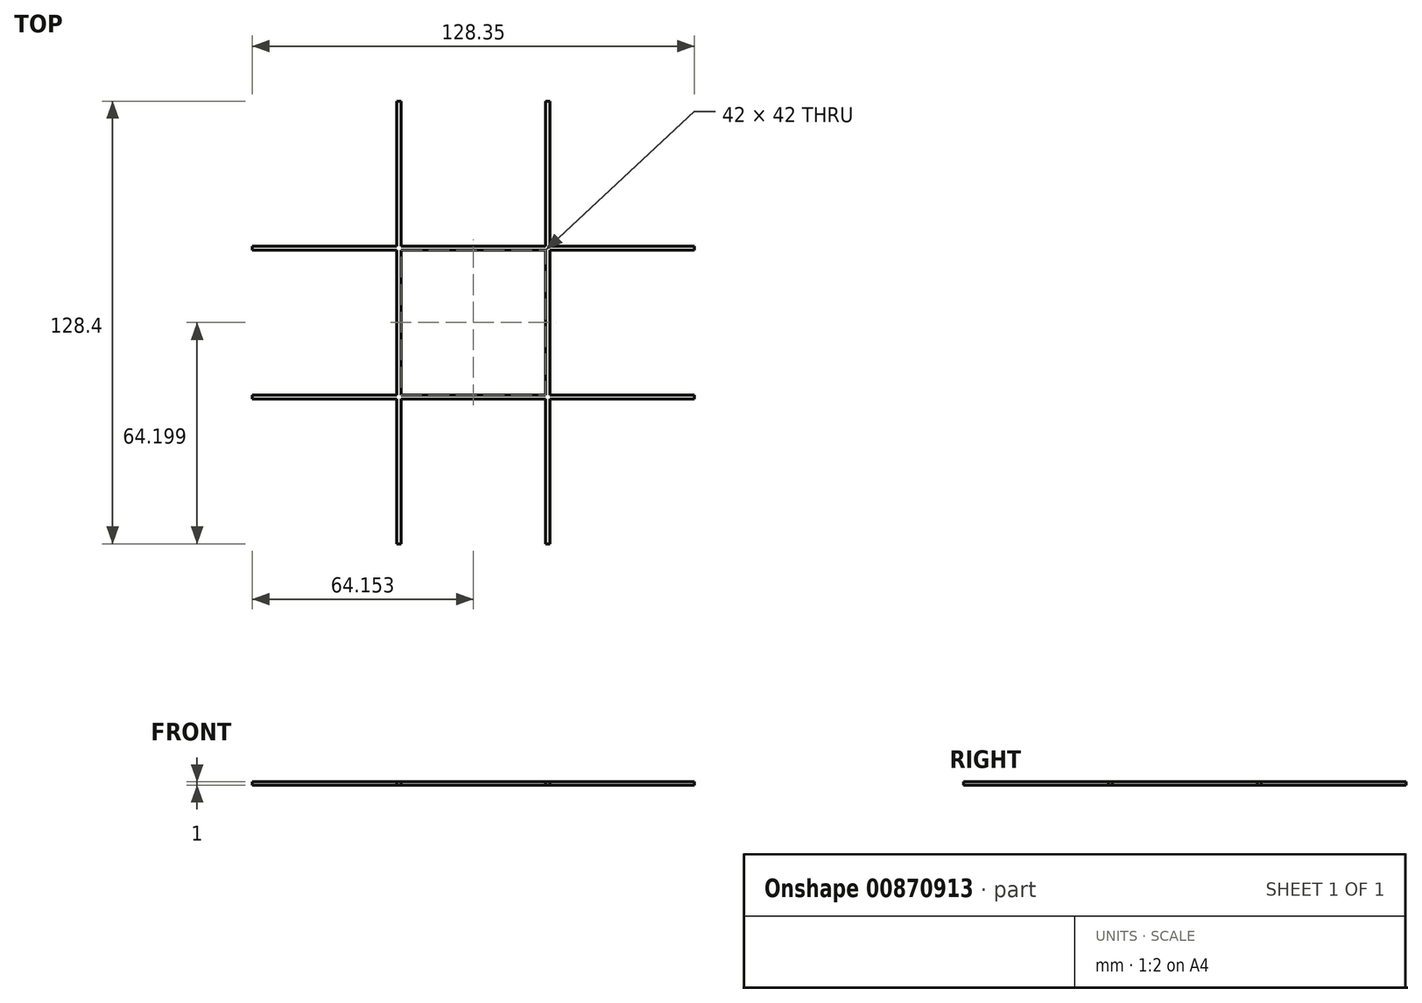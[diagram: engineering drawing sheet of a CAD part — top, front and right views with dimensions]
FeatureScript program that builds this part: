
annotation { "Feature Type Name" : "Feature", "Feature Type Description" : "" }
export const myFeature = defineFeature(function(context is Context, id is Id, definition is map)
    precondition{}
    {
        {
            var Q0;
            Q0=qCreatedBy(makeId("Top.planeOp"),FACE);
            var sketch = newSketch(context, id + "F0", { "sketchPlane" : qUnion([Q0])});
            skLineSegment(sketch, "E0.bottom", {"start": v(-34.17, 34.2) * mm, "end": v(7.83, 34.2) * mm});
            skLineSegment(sketch, "E0.top", {"start": v(-34.17, -7.8) * mm, "end": v(7.83, -7.8) * mm});
            skLineSegment(sketch, "E0.left", {"start": v(-34.17, 34.2) * mm, "end": v(-34.17, -7.8) * mm});
            skLineSegment(sketch, "E0.right", {"start": v(7.83, 34.2) * mm, "end": v(7.83, -7.8) * mm});
            skLineSegment(sketch, "E1.bottom", {"start": v(-35.37, 35.4) * mm, "end": v(9.03, 35.4) * mm});
            skLineSegment(sketch, "E1.top", {"start": v(-35.37, -9) * mm, "end": v(9.03, -9) * mm});
            skLineSegment(sketch, "E1.left", {"start": v(-35.37, 35.4) * mm, "end": v(-35.37, -9) * mm});
            skLineSegment(sketch, "E1.right", {"start": v(9.03, 35.4) * mm, "end": v(9.03, -9) * mm});
            skSolve(sketch);
        }
        {
            var Q0;
            Q0=makeQuery(id+"F0.imprint","IMPRINT",FACE,{"disambiguationData":[TD([[makeQuery(id+"F0.imprint","IMPRINT",EDGE,{"derivedFrom":sQuery(id+"F0.wireOp",EDGE,"E0.bottom")}),1.0]])]});
            extrude(context, id + "F1", {"entities" : qUnion([Q0]), "depth" : 1 * mm, "offsetDistance" : 25.4 * mm});
        }
        {
            var Q0;
            Q0=makeQuery(id+"F1.opExtrude","SWEPT_BODY",BODY,{"disambiguationData":[OSD([sQuery(id+"F0.wireOp",EDGE,"E0.bottom"),sQuery(id+"F0.wireOp",EDGE,"E0.top"),sQuery(id+"F0.wireOp",EDGE,"E0.left"),sQuery(id+"F0.wireOp",EDGE,"E0.right"),sQuery(id+"F0.wireOp",EDGE,"E1.bottom"),sQuery(id+"F0.wireOp",EDGE,"E1.top"),sQuery(id+"F0.wireOp",EDGE,"E1.left"),sQuery(id+"F0.wireOp",EDGE,"E1.right")])]});
            transform(context, id + "F2", {"entities" : qUnion([Q0]), "transformType" : TransformType.TRANSLATION_3D, "dx" : 43.2 * mm, "dy" : 0 * mm, "dz" : 0 * mm, "makeCopy" : true});
        }
        {
            var Q0;
            Q0=makeQuery(id+"F2.opPattern","COPY",BODY,{"derivedFrom":makeQuery(id+"Fn17MzBWq50HigD_0.opExtrude","SWEPT_BODY",BODY,{"disambiguationData":[OSD([sQuery(id+"F0.wireOp",EDGE,"E0.bottom"),sQuery(id+"F0.wireOp",EDGE,"E0.top"),sQuery(id+"F0.wireOp",EDGE,"E0.left"),sQuery(id+"F0.wireOp",EDGE,"E0.right"),sQuery(id+"F0.wireOp",EDGE,"E1.bottom"),sQuery(id+"F0.wireOp",EDGE,"E1.top"),sQuery(id+"F0.wireOp",EDGE,"E1.left"),sQuery(id+"F0.wireOp",EDGE,"E1.right")])]}),"instanceName":"1"});
            var Q1;
            Q1=makeQuery(id+"F2.opPattern","COPY",BODY,{"derivedFrom":makeQuery(id+"F1.opExtrude","SWEPT_BODY",BODY,{"disambiguationData":[OSD([sQuery(id+"F0.wireOp",EDGE,"E0.bottom"),sQuery(id+"F0.wireOp",EDGE,"E0.top"),sQuery(id+"F0.wireOp",EDGE,"E0.left"),sQuery(id+"F0.wireOp",EDGE,"E0.right"),sQuery(id+"F0.wireOp",EDGE,"E1.bottom"),sQuery(id+"F0.wireOp",EDGE,"E1.top"),sQuery(id+"F0.wireOp",EDGE,"E1.left"),sQuery(id+"F0.wireOp",EDGE,"E1.right")])]}),"instanceName":"1"});
            transform(context, id + "F3", {"entities" : qUnion([Q0, Q1]), "transformType" : TransformType.TRANSLATION_3D, "dx" : 43.2 * mm, "dy" : 0 * mm, "dz" : 0 * mm, "makeCopy" : true});
        }
        {
            var Q0;
            Q0=makeQuery(id+"F1.opExtrude","SWEPT_BODY",BODY,{"disambiguationData":[OSD([sQuery(id+"F0.wireOp",EDGE,"E0.bottom"),sQuery(id+"F0.wireOp",EDGE,"E0.top"),sQuery(id+"F0.wireOp",EDGE,"E0.left"),sQuery(id+"F0.wireOp",EDGE,"E0.right"),sQuery(id+"F0.wireOp",EDGE,"E1.bottom"),sQuery(id+"F0.wireOp",EDGE,"E1.top"),sQuery(id+"F0.wireOp",EDGE,"E1.left"),sQuery(id+"F0.wireOp",EDGE,"E1.right")])]});
            var Q1;
            Q1=makeQuery(id+"F2.opPattern","COPY",BODY,{"derivedFrom":makeQuery(id+"F1.opExtrude","SWEPT_BODY",BODY,{"disambiguationData":[OSD([sQuery(id+"F0.wireOp",EDGE,"E0.bottom"),sQuery(id+"F0.wireOp",EDGE,"E0.top"),sQuery(id+"F0.wireOp",EDGE,"E0.left"),sQuery(id+"F0.wireOp",EDGE,"E0.right"),sQuery(id+"F0.wireOp",EDGE,"E1.bottom"),sQuery(id+"F0.wireOp",EDGE,"E1.top"),sQuery(id+"F0.wireOp",EDGE,"E1.left"),sQuery(id+"F0.wireOp",EDGE,"E1.right")])]}),"instanceName":"1"});
            var Q2;
            Q2=makeQuery(id+"F3.opPattern","COPY",BODY,{"derivedFrom":makeQuery(id+"F2.opPattern","COPY",BODY,{"derivedFrom":makeQuery(id+"F1.opExtrude","SWEPT_BODY",BODY,{"disambiguationData":[OSD([sQuery(id+"F0.wireOp",EDGE,"E0.bottom"),sQuery(id+"F0.wireOp",EDGE,"E0.top"),sQuery(id+"F0.wireOp",EDGE,"E0.left"),sQuery(id+"F0.wireOp",EDGE,"E0.right"),sQuery(id+"F0.wireOp",EDGE,"E1.bottom"),sQuery(id+"F0.wireOp",EDGE,"E1.top"),sQuery(id+"F0.wireOp",EDGE,"E1.left"),sQuery(id+"F0.wireOp",EDGE,"E1.right")])]}),"instanceName":"1"}),"instanceName":"1"});
            booleanBodies(context, id + "F4", {"operationType" : BooleanOperationType.UNION, "tools" : qUnion([Q0, Q1, Q2])});
        }
        {
            var Q0;
            Q0=makeQuery(id+"F1.opExtrude","SWEPT_BODY",BODY,{"disambiguationData":[OSD([sQuery(id+"F0.wireOp",EDGE,"E0.bottom"),sQuery(id+"F0.wireOp",EDGE,"E0.top"),sQuery(id+"F0.wireOp",EDGE,"E0.left"),sQuery(id+"F0.wireOp",EDGE,"E0.right"),sQuery(id+"F0.wireOp",EDGE,"E1.bottom"),sQuery(id+"F0.wireOp",EDGE,"E1.top"),sQuery(id+"F0.wireOp",EDGE,"E1.left"),sQuery(id+"F0.wireOp",EDGE,"E1.right")])]});
            transform(context, id + "F5", {"entities" : qUnion([Q0]), "transformType" : TransformType.TRANSLATION_3D, "dx" : 0 * mm, "dy" : 43.2 * mm, "dz" : 0 * mm, "makeCopy" : true});
        }
        {
            var Q0;
            Q0=makeQuery(id+"F5.opPattern","COPY",BODY,{"derivedFrom":makeQuery(id+"Fn17MzBWq50HigD_0.opExtrude","SWEPT_BODY",BODY,{"disambiguationData":[OSD([sQuery(id+"F0.wireOp",EDGE,"E0.bottom"),sQuery(id+"F0.wireOp",EDGE,"E0.top"),sQuery(id+"F0.wireOp",EDGE,"E0.left"),sQuery(id+"F0.wireOp",EDGE,"E0.right"),sQuery(id+"F0.wireOp",EDGE,"E1.bottom"),sQuery(id+"F0.wireOp",EDGE,"E1.top"),sQuery(id+"F0.wireOp",EDGE,"E1.left"),sQuery(id+"F0.wireOp",EDGE,"E1.right")])]}),"instanceName":"1"});
            var Q1;
            Q1=makeQuery(id+"F5.opPattern","COPY",BODY,{"derivedFrom":makeQuery(id+"F1.opExtrude","SWEPT_BODY",BODY,{"disambiguationData":[OSD([sQuery(id+"F0.wireOp",EDGE,"E0.bottom"),sQuery(id+"F0.wireOp",EDGE,"E0.top"),sQuery(id+"F0.wireOp",EDGE,"E0.left"),sQuery(id+"F0.wireOp",EDGE,"E0.right"),sQuery(id+"F0.wireOp",EDGE,"E1.bottom"),sQuery(id+"F0.wireOp",EDGE,"E1.top"),sQuery(id+"F0.wireOp",EDGE,"E1.left"),sQuery(id+"F0.wireOp",EDGE,"E1.right")])]}),"instanceName":"1"});
            transform(context, id + "F6", {"entities" : qUnion([Q0, Q1]), "transformType" : TransformType.TRANSLATION_3D, "dx" : 0 * mm, "dy" : 43.2 * mm, "dz" : 0 * mm, "makeCopy" : true});
        }
        {
            var Q0;
            Q0=makeQuery(id+"F1.opExtrude","SWEPT_BODY",BODY,{"disambiguationData":[OSD([sQuery(id+"F0.wireOp",EDGE,"E0.bottom"),sQuery(id+"F0.wireOp",EDGE,"E0.top"),sQuery(id+"F0.wireOp",EDGE,"E0.left"),sQuery(id+"F0.wireOp",EDGE,"E0.right"),sQuery(id+"F0.wireOp",EDGE,"E1.bottom"),sQuery(id+"F0.wireOp",EDGE,"E1.top"),sQuery(id+"F0.wireOp",EDGE,"E1.left"),sQuery(id+"F0.wireOp",EDGE,"E1.right")])]});
            var Q1;
            Q1=makeQuery(id+"F5.opPattern","COPY",BODY,{"derivedFrom":makeQuery(id+"F1.opExtrude","SWEPT_BODY",BODY,{"disambiguationData":[OSD([sQuery(id+"F0.wireOp",EDGE,"E0.bottom"),sQuery(id+"F0.wireOp",EDGE,"E0.top"),sQuery(id+"F0.wireOp",EDGE,"E0.left"),sQuery(id+"F0.wireOp",EDGE,"E0.right"),sQuery(id+"F0.wireOp",EDGE,"E1.bottom"),sQuery(id+"F0.wireOp",EDGE,"E1.top"),sQuery(id+"F0.wireOp",EDGE,"E1.left"),sQuery(id+"F0.wireOp",EDGE,"E1.right")])]}),"instanceName":"1"});
            var Q2;
            Q2=makeQuery(id+"F6.opPattern","COPY",BODY,{"derivedFrom":makeQuery(id+"F5.opPattern","COPY",BODY,{"derivedFrom":makeQuery(id+"F1.opExtrude","SWEPT_BODY",BODY,{"disambiguationData":[OSD([sQuery(id+"F0.wireOp",EDGE,"E0.bottom"),sQuery(id+"F0.wireOp",EDGE,"E0.top"),sQuery(id+"F0.wireOp",EDGE,"E0.left"),sQuery(id+"F0.wireOp",EDGE,"E0.right"),sQuery(id+"F0.wireOp",EDGE,"E1.bottom"),sQuery(id+"F0.wireOp",EDGE,"E1.top"),sQuery(id+"F0.wireOp",EDGE,"E1.left"),sQuery(id+"F0.wireOp",EDGE,"E1.right")])]}),"instanceName":"1"}),"instanceName":"1"});
            booleanBodies(context, id + "F7", {"operationType" : BooleanOperationType.UNION, "tools" : qUnion([Q0, Q1, Q2])});
        }
        {
            var Q0;
            {var subQ0=makeQuery(id+"F1.opExtrude","CAP_FACE",FACE,{"disambiguationData":[OSD([sQuery(id+"F0.wireOp",EDGE,"E0.bottom"),sQuery(id+"F0.wireOp",EDGE,"E0.top"),sQuery(id+"F0.wireOp",EDGE,"E0.left"),sQuery(id+"F0.wireOp",EDGE,"E0.right"),sQuery(id+"F0.wireOp",EDGE,"E1.bottom"),sQuery(id+"F0.wireOp",EDGE,"E1.top"),sQuery(id+"F0.wireOp",EDGE,"E1.left"),sQuery(id+"F0.wireOp",EDGE,"E1.right")])],"isStart":false});var subQ1=makeQuery(id+"F2.opPattern","COPY",FACE,{"derivedFrom":subQ0,"instanceName":"1"});var subQ2=makeQuery(id+"F4.opBoolean","MERGE",FACE,{"derivedFrom":[subQ0,subQ1,makeQuery(id+"F3.opPattern","COPY",FACE,{"derivedFrom":subQ1,"instanceName":"1"})]});var subQ3=makeQuery(id+"F5.opPattern","COPY",FACE,{"derivedFrom":subQ2,"instanceName":"1"});Q0=makeQuery(id+"F7.opBoolean","MERGE",FACE,{"derivedFrom":[subQ2,subQ3,makeQuery(id+"F6.opPattern","COPY",FACE,{"derivedFrom":subQ3,"instanceName":"1"})]});}
            var sketch = newSketch(context, id + "F8", { "sketchPlane" : qUnion([Q0])});
            skLineSegment(sketch, "E2", {"start": v(-34.17, -7.8) * mm, "end": v(-36.03, -7.8) * mm});
            skLineSegment(sketch, "E3", {"start": v(-36.03, -7.8) * mm, "end": v(-36.03, -10.02) * mm});
            skLineSegment(sketch, "E4", {"start": v(-36.03, -10.02) * mm, "end": v(98.96, -10.02) * mm});
            skLineSegment(sketch, "E5", {"start": v(98.96, -10.02) * mm, "end": v(98.96, -7.8) * mm});
            skLineSegment(sketch, "E6", {"start": v(98.96, -7.8) * mm, "end": v(-34.03, -7.8) * mm});
            skLineSegment(sketch, "E7", {"start": v(-34.03, -7.8) * mm, "end": v(-36.03, -7.8) * mm});
            skLineSegment(sketch, "E8", {"start": v(-34.17, -7.8) * mm, "end": v(-34.03, 122.86) * mm});
            skLineSegment(sketch, "E9", {"start": v(-34.03, 122.86) * mm, "end": v(-37.08, 122.87) * mm});
            skLineSegment(sketch, "E10", {"start": v(-37.08, 122.87) * mm, "end": v(-36.03, -7.8) * mm});
            skLineSegment(sketch, "E11", {"start": v(94.23, 120.6) * mm, "end": v(96.03, 120.6) * mm});
            skLineSegment(sketch, "E12", {"start": v(96.03, 120.6) * mm, "end": v(96.03, 122.44) * mm});
            skLineSegment(sketch, "E13", {"start": v(96.03, 122.44) * mm, "end": v(-37.08, 122.87) * mm});
            skLineSegment(sketch, "E14", {"start": v(94.23, 120.6) * mm, "end": v(-34.17, 120.6) * mm});
            skLineSegment(sketch, "E15", {"start": v(-34.17, 120.6) * mm, "end": v(-37.06, 120.59) * mm});
            skLineSegment(sketch, "E16", {"start": v(94.23, 120.6) * mm, "end": v(94.23, -7.8) * mm});
            skLineSegment(sketch, "E17", {"start": v(94.23, -7.8) * mm, "end": v(97.23, -7.8) * mm});
            skLineSegment(sketch, "E18", {"start": v(97.23, -7.8) * mm, "end": v(96.03, 120.6) * mm});
            skSolve(sketch);
        }
        {
            var Q0;
            {var subQ0=sQuery(id+"F8.wireOp",EDGE,"E14");var subQ1=makeQuery(id+"F1.opExtrude","CAP_EDGE",EDGE,{"disambiguationData":[OSD([sQuery(id+"F0.wireOp",EDGE,"E0.right")])],"isStart":false});var subQ2=makeQuery(id+"F8.imprint","INTERSECT",VERTEX,{"derivedFrom":[makeQuery(id+"F6.opPattern","COPY",EDGE,{"derivedFrom":makeQuery(id+"F5.opPattern","COPY",EDGE,{"derivedFrom":makeQuery(id+"F2.opPattern","COPY",EDGE,{"derivedFrom":subQ1,"instanceName":"1"}),"instanceName":"1"}),"instanceName":"1"}),subQ0]});var subQ3=makeQuery(id+"F1.opExtrude","CAP_EDGE",EDGE,{"disambiguationData":[OSD([sQuery(id+"F0.wireOp",EDGE,"E1.right")])],"isStart":false});var subQ5=makeQuery(id+"F2.opPattern","COPY",EDGE,{"derivedFrom":subQ3,"instanceName":"1"});var subQ15=makeQuery(id+"F8.imprint","INTERSECT",VERTEX,{"derivedFrom":[makeQuery(id+"F6.opPattern","COPY",EDGE,{"derivedFrom":makeQuery(id+"F5.opPattern","COPY",EDGE,{"derivedFrom":subQ5,"instanceName":"1"}),"instanceName":"1"}),subQ0]});Q0=makeQuery(id+"F8.imprint","IMPRINT",FACE,{"disambiguationData":[TD([[makeQuery(id+"F8.imprint","IMPRINT",EDGE,{"disambiguationData":[TD([[subQ2,1.0],[subQ15,-1.0]])],"derivedFrom":subQ0}),-1.0]])]});}
            var Q1;
            {var subQ0=sQuery(id+"F8.wireOp",EDGE,"E16");var subQ1=sQuery(id+"F0.wireOp",EDGE,"E0.bottom");var subQ2=makeQuery(id+"F3.opPattern","COPY",EDGE,{"derivedFrom":makeQuery(id+"F2.opPattern","COPY",EDGE,{"derivedFrom":makeQuery(id+"F1.opExtrude","CAP_EDGE",EDGE,{"disambiguationData":[OSD([subQ1])],"isStart":false}),"instanceName":"1"}),"instanceName":"1"});var subQ3=makeQuery(id+"F8.imprint","INTERSECT",VERTEX,{"derivedFrom":[subQ2,subQ0]});Q1=makeQuery(id+"F8.imprint","IMPRINT",FACE,{"disambiguationData":[TD([[makeQuery(id+"F8.imprint","IMPRINT",EDGE,{"disambiguationData":[TD([[subQ3,-1.0]])],"derivedFrom":subQ0}),1.0]])]});}
            var Q2;
            {var subQ0=sQuery(id+"F8.wireOp",EDGE,"E18");Q2=makeQuery(id+"F8.imprint","IMPRINT",FACE,{"disambiguationData":[TD([[makeQuery(id+"F8.imprint","IMPRINT",EDGE,{"derivedFrom":subQ0}),1.0]])]});}
            var Q3;
            {var subQ1=sQuery(id+"F8.wireOp",EDGE,"E12");Q3=makeQuery(id+"F8.imprint","IMPRINT",FACE,{"disambiguationData":[TD([[makeQuery(id+"F8.imprint","IMPRINT",EDGE,{"derivedFrom":subQ1}),1.0]])]});}
            var Q4;
            {var subQ4=sQuery(id+"F8.wireOp",EDGE,"E3");Q4=makeQuery(id+"F8.imprint","IMPRINT",FACE,{"disambiguationData":[TD([[makeQuery(id+"F8.imprint","IMPRINT",EDGE,{"derivedFrom":subQ4}),1.0]])]});}
            var Q5;
            {var subQ8=makeQuery(id+"F1.opExtrude","CAP_EDGE",EDGE,{"disambiguationData":[OSD([sQuery(id+"F0.wireOp",EDGE,"E1.top")])],"isStart":false});var subQ9=makeQuery(id+"F2.opPattern","COPY",EDGE,{"derivedFrom":subQ8,"instanceName":"1"});var subQ10=makeQuery(id+"F4.opBoolean","MERGE",EDGE,{"derivedFrom":[subQ8,subQ9,makeQuery(id+"F3.opPattern","COPY",EDGE,{"derivedFrom":subQ9,"instanceName":"1"})]});Q5=makeQuery(id+"F8.imprint","IMPRINT",FACE,{"disambiguationData":[TD([[makeQuery(id+"F8.imprint","IMPRINT",EDGE,{"derivedFrom":subQ10}),1.0]])]});}
            var Q6;
            {var subQ0=sQuery(id+"F0.wireOp",EDGE,"E0.left");var subQ1=makeQuery(id+"F1.opExtrude","CAP_EDGE",EDGE,{"disambiguationData":[OSD([subQ0])],"isStart":false});Q6=makeQuery(id+"F8.imprint","IMPRINT",FACE,{"disambiguationData":[TD([[makeQuery(id+"F8.imprint","IMPRINT",EDGE,{"derivedFrom":subQ1}),-1.0]])]});}
            var Q7;
            {var subQ0=sQuery(id+"F8.wireOp",EDGE,"E10");var subQ7=sQuery(id+"F8.wireOp",EDGE,"E15");var subQ9=makeQuery(id+"F8.imprint","INTERSECT",VERTEX,{"derivedFrom":[subQ0,subQ7]});Q7=makeQuery(id+"F8.imprint","IMPRINT",FACE,{"disambiguationData":[TD([[makeQuery(id+"F8.imprint","IMPRINT",EDGE,{"disambiguationData":[TD([[subQ9,-1.0]])],"derivedFrom":subQ0}),1.0]])]});}
            var Q8;
            {var subQ0=sQuery(id+"F8.wireOp",EDGE,"E15");var subQ1=sQuery(id+"F8.wireOp",EDGE,"E14");var subQ2=makeQuery(id+"F8.imprint","INTERSECT",VERTEX,{"derivedFrom":[makeQuery(id+"F6.opPattern","COPY",EDGE,{"derivedFrom":makeQuery(id+"F5.opPattern","COPY",EDGE,{"derivedFrom":makeQuery(id+"F1.opExtrude","CAP_EDGE",EDGE,{"disambiguationData":[OSD([sQuery(id+"F0.wireOp",EDGE,"E0.left")])],"isStart":false}),"instanceName":"1"}),"instanceName":"1"}),subQ1,subQ0]});var subQ7=sQuery(id+"F8.wireOp",EDGE,"E8");var subQ8=makeQuery(id+"F8.imprint","INTERSECT",VERTEX,{"derivedFrom":[subQ7,subQ1]});Q8=makeQuery(id+"F8.imprint","IMPRINT",FACE,{"disambiguationData":[TD([[makeQuery(id+"F8.imprint","IMPRINT",EDGE,{"disambiguationData":[TD([[subQ2,-1.0],[subQ8,1.0]])],"derivedFrom":subQ1}),1.0]])]});}
            var Q9;
            {var subQ0=sQuery(id+"F8.wireOp",EDGE,"E15");var subQ1=sQuery(id+"F8.wireOp",EDGE,"E10");var subQ2=makeQuery(id+"F8.imprint","INTERSECT",VERTEX,{"derivedFrom":[subQ1,subQ0]});Q9=makeQuery(id+"F8.imprint","IMPRINT",FACE,{"disambiguationData":[TD([[makeQuery(id+"F8.imprint","IMPRINT",EDGE,{"disambiguationData":[TD([[subQ2,1.0]])],"derivedFrom":subQ1}),1.0]])]});}
            extrude(context, id + "F9", {"entities" : qUnion([Q0, Q1, Q2, Q3, Q4, Q5, Q6, Q7, Q8, Q9]), "operationType" : NewBodyOperationType.REMOVE, "oppositeDirection" : true, "depth" : 25.4 * mm, "offsetDistance" : 25.4 * mm});
        }
    });
